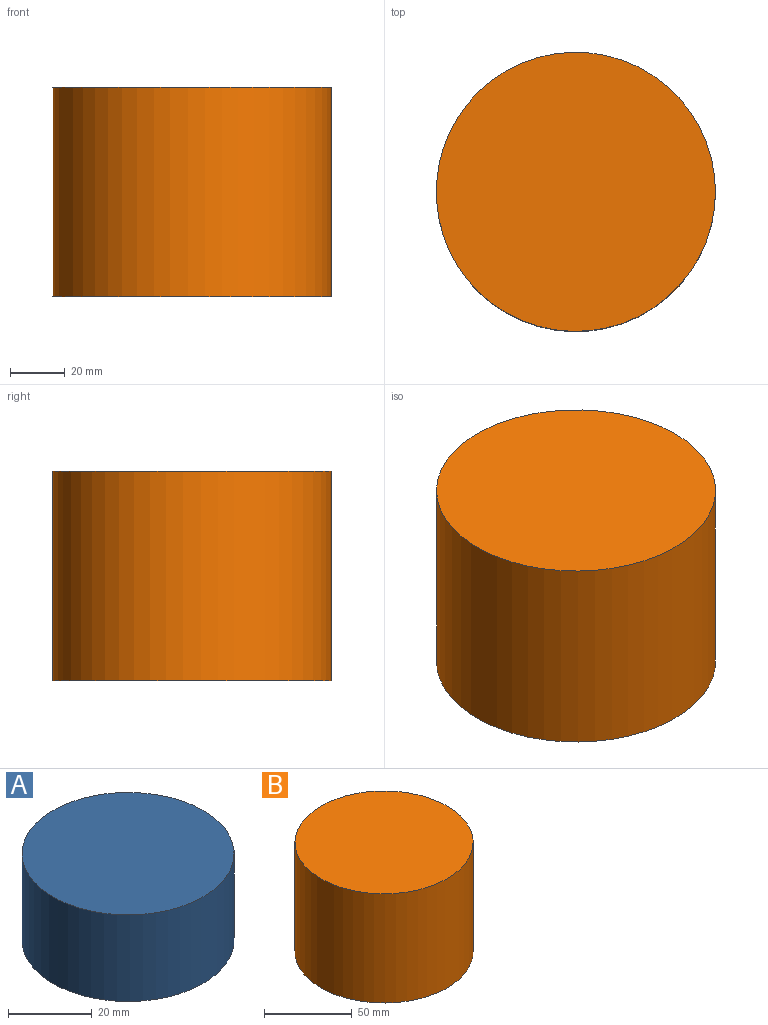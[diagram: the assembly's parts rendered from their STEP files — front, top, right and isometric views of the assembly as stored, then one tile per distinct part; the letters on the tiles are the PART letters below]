
ASSEMBLY  parts=2 mates=1
PART A: 5 faces, bbox 50.8x50.8x25.4 mm
  f0: cylinder r=25.4mm len=50.8mm, axis (0,0,-1), area 4053.7mm2, adj f1,f2
  f1: plane 50.8x50.8mm, normal (0,0,1), area 2026.8mm2, adj f0
  f2: plane 50.8x50.8mm, normal (0,0,-1), area 886.7mm2, adj f0,f3
  f3: cylinder r=19.05mm len=38.1mm, axis (0,0,-1), area 2280.2mm2, adj f2,f4
  f4: plane 38.1x38.1mm, normal (0,0,-1), area 1140.1mm2, adj f3
PART B: 5 faces, bbox 101.6x101.6x76.2 mm
  f0: cylinder r=50.8mm len=101.6mm, axis (0,0,-1), area 24322mm2, adj f1,f2
  f1: plane 101.6x101.6mm, normal (0,0,1), area 8107.3mm2, adj f0
  f2: plane 101.6x101.6mm, normal (0,0,-1), area 1900.2mm2, adj f0,f3
  f3: cylinder r=44.45mm len=88.9mm, axis (0,0,-1), area 19508.2mm2, adj f2,f4
  f4: plane 88.9x88.9mm, normal (0,0,-1), area 6207.2mm2, adj f3
PLACE A t=(-33.6,27.39,-33.13)mm
PLACE B t=(27.17,-36.15,-33.13)mm
MATE slider A.f0 <-> B.f0  axis (0,0,-1) through (-2.16,-13.76,-33.13)mm
